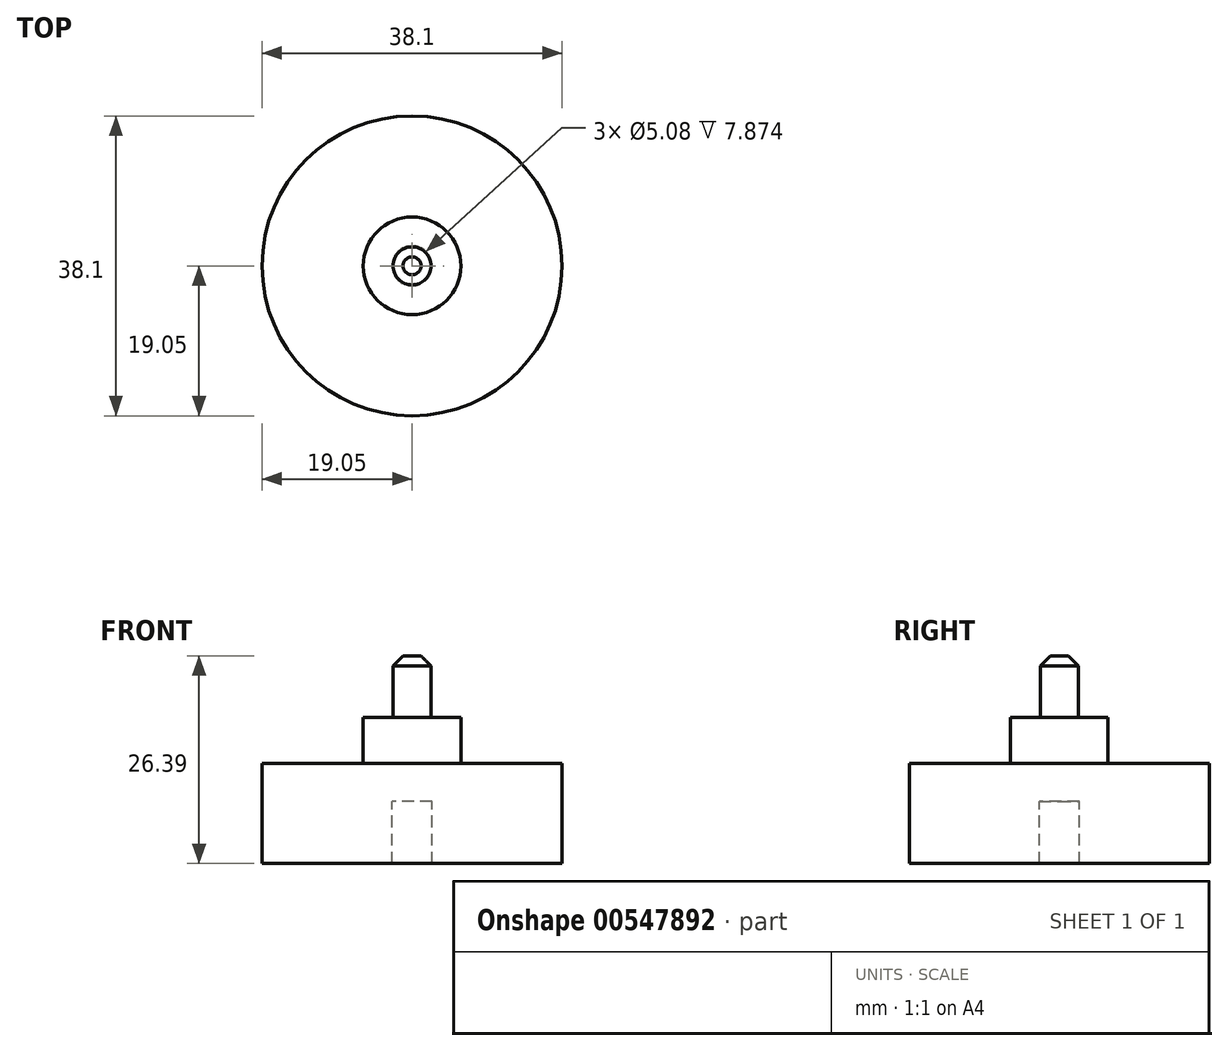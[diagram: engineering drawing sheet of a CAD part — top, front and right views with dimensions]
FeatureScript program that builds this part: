
annotation { "Feature Type Name" : "Feature", "Feature Type Description" : "" }
export const myFeature = defineFeature(function(context is Context, id is Id, definition is map)
    precondition{}
    {
        {
            var Q0;
            Q0=qCreatedBy(makeId("Front.planeOp"),FACE);
            var sketch = newSketch(context, id + "F0", { "sketchPlane" : qUnion([Q0])});
            skLineSegment(sketch, "E0", {"start": v(19.05, 0) * mm, "end": v(19.05, 12.7) * mm});
            skLineSegment(sketch, "E1", {"start": v(6.2, 18.54) * mm, "end": v(6.2, 12.7) * mm});
            skLineSegment(sketch, "E2", {"start": v(19.05, 12.7) * mm, "end": v(6.2, 12.7) * mm});
            skLineSegment(sketch, "E3", {"start": v(2.54, 0) * mm, "end": v(2.54, 7.87) * mm});
            skLineSegment(sketch, "E4", {"start": v(2.54, 7.87) * mm, "end": v(0, 7.87) * mm});
            skLineSegment(sketch, "E5", {"start": v(19.05, 0) * mm, "end": v(2.54, 0) * mm});
            skLineSegment(sketch, "E6", {"start": v(0, 26.4) * mm, "end": v(0, 7.87) * mm});
            skLineSegment(sketch, "E7", {"start": v(0, 26.4) * mm, "end": v(2.41, 26.4) * mm});
            skLineSegment(sketch, "E8", {"start": v(2.41, 26.4) * mm, "end": v(2.41, 18.54) * mm});
            skLineSegment(sketch, "E9", {"start": v(6.2, 18.54) * mm, "end": v(2.41, 18.54) * mm});
            skPoint(sketch, "E9.endSnap0", {"position": v(2.41, 20.84) * mm});
            skPoint(sketch, "E10.orphan", {"position": v(2.41, 15.29) * mm});
            skSolve(sketch);
        }
        {
            var Q0;
            Q0 = qSketchRegion(id + "F0", true);
            var Q1;
            Q1=sQuery(id+"F0.wireOp",EDGE,"E6");
            revolve(context, id + "F1", {"entities" : qUnion([Q0]), "axis" : qUnion([Q1]), "revolveType" : RevolveType.FULL});
        }
        {
            var Q0;
            Q0=makeQuery(id+"F1.opRevolve","SWEPT_EDGE",EDGE,{"disambiguationData":[OSD([sQuery(id+"F0.wireOp",EDGE,"E7"),sQuery(id+"F0.wireOp",EDGE,"E8")])]});
            chamfer(context, id + "F2", {"entities" : qUnion([Q0]), "width" : 1.27 * mm, "tangentPropagation" : true});
        }
    });
